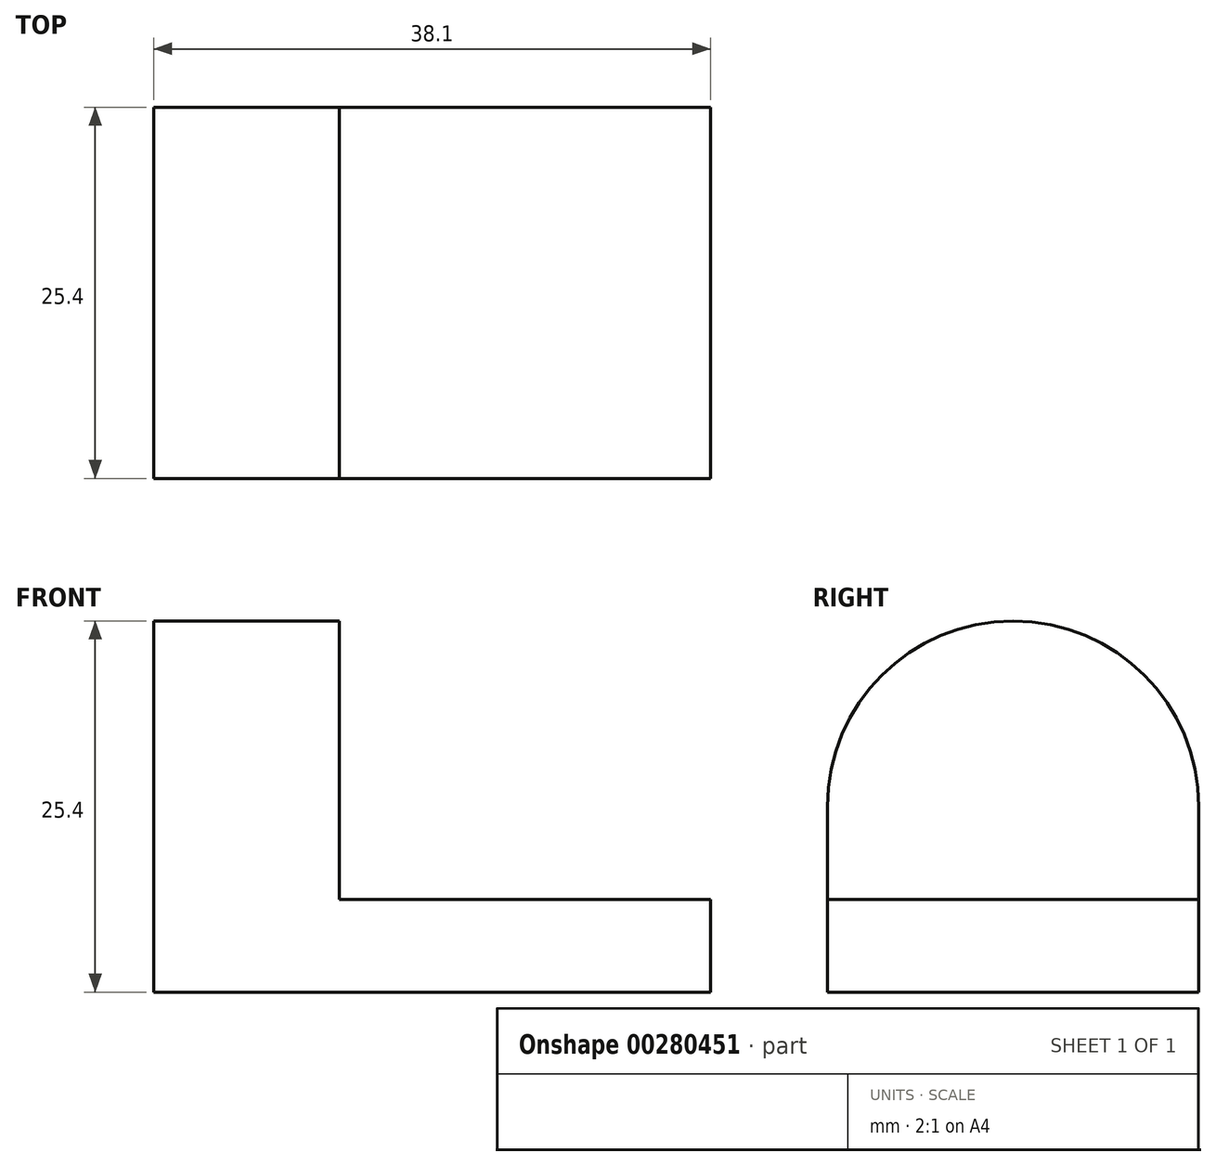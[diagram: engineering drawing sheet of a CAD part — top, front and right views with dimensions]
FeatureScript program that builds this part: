
annotation { "Feature Type Name" : "Feature", "Feature Type Description" : "" }
export const myFeature = defineFeature(function(context is Context, id is Id, definition is map)
    precondition{}
    {
        {
            var Q0;
            Q0=qCreatedBy(makeId("Front.planeOp"),FACE);
            var sketch = newSketch(context, id + "F0", { "sketchPlane" : qUnion([Q0])});
            skLineSegment(sketch, "E0", {"start": v(0, 0) * mm, "end": v(0, 25.4) * mm});
            skLineSegment(sketch, "E1", {"start": v(0, 25.4) * mm, "end": v(12.7, 25.4) * mm});
            skLineSegment(sketch, "E2", {"start": v(12.7, 25.4) * mm, "end": v(12.7, 6.35) * mm});
            skLineSegment(sketch, "E3", {"start": v(12.7, 6.35) * mm, "end": v(38.1, 6.35) * mm});
            skLineSegment(sketch, "E4", {"start": v(38.1, 6.35) * mm, "end": v(38.1, 0) * mm});
            skLineSegment(sketch, "E5", {"start": v(38.1, 0) * mm, "end": v(0, 0) * mm});
            skSolve(sketch);
        }
        {
            var Q0;
            Q0 = qSketchRegion(id + "F0", true);
            extrude(context, id + "F1", {"entities" : qUnion([Q0]), "oppositeDirection" : true, "depth" : 25.4 * mm});
        }
        {
            var Q0;
            Q0=makeQuery(id+"F1.opExtrude","SWEPT_FACE",FACE,{"disambiguationData":[OSD([sQuery(id+"F0.wireOp",EDGE,"E2")])]});
            var sketch = newSketch(context, id + "F2", { "sketchPlane" : qUnion([Q0])});
            skLineSegment(sketch, "E6", {"start": v(0, 12.7) * mm, "end": v(0, 12.7) * mm});
            skLineSegment(sketch, "E7", {"start": v(12.7, 25.4) * mm, "end": v(12.7, 25.4) * mm});
            skPoint(sketch, "E8.visualSharp", {"position": v(0, 25.4) * mm});
            skArc(sketch, "E8.filletArc", {"start": v(12.7, 25.4) * mm, "mid": v(3.72, 21.68) * mm, "end": v(0, 12.7) * mm});
            skLineSegment(sketch, "E9", {"start": v(25.4, 12.7) * mm, "end": v(25.4, 12.7) * mm});
            skPoint(sketch, "E10.visualSharp", {"position": v(25.4, 25.4) * mm});
            skArc(sketch, "E10.filletArc", {"start": v(25.4, 12.7) * mm, "mid": v(21.68, 21.68) * mm, "end": v(12.7, 25.4) * mm});
            skSolve(sketch);
        }
        {
            var Q0;
            {var subQ0=sQuery(id+"F2.wireOp",EDGE,"E8.filletArc");Q0=makeQuery(id+"F2.imprint","IMPRINT",FACE,{"disambiguationData":[TD([[makeQuery(id+"F2.imprint","IMPRINT",EDGE,{"derivedFrom":subQ0}),-1.0]])]});}
            var Q1;
            {var subQ0=sQuery(id+"F2.wireOp",EDGE,"E10.filletArc");Q1=makeQuery(id+"F2.imprint","IMPRINT",FACE,{"disambiguationData":[TD([[makeQuery(id+"F2.imprint","IMPRINT",EDGE,{"derivedFrom":subQ0}),-1.0]])]});}
            extrude(context, id + "F3", {"entities" : qUnion([Q0, Q1]), "operationType" : NewBodyOperationType.REMOVE, "endBound" : BoundingType.THROUGH_ALL, "oppositeDirection" : true, "depth" : 25.4 * mm});
        }
    });
